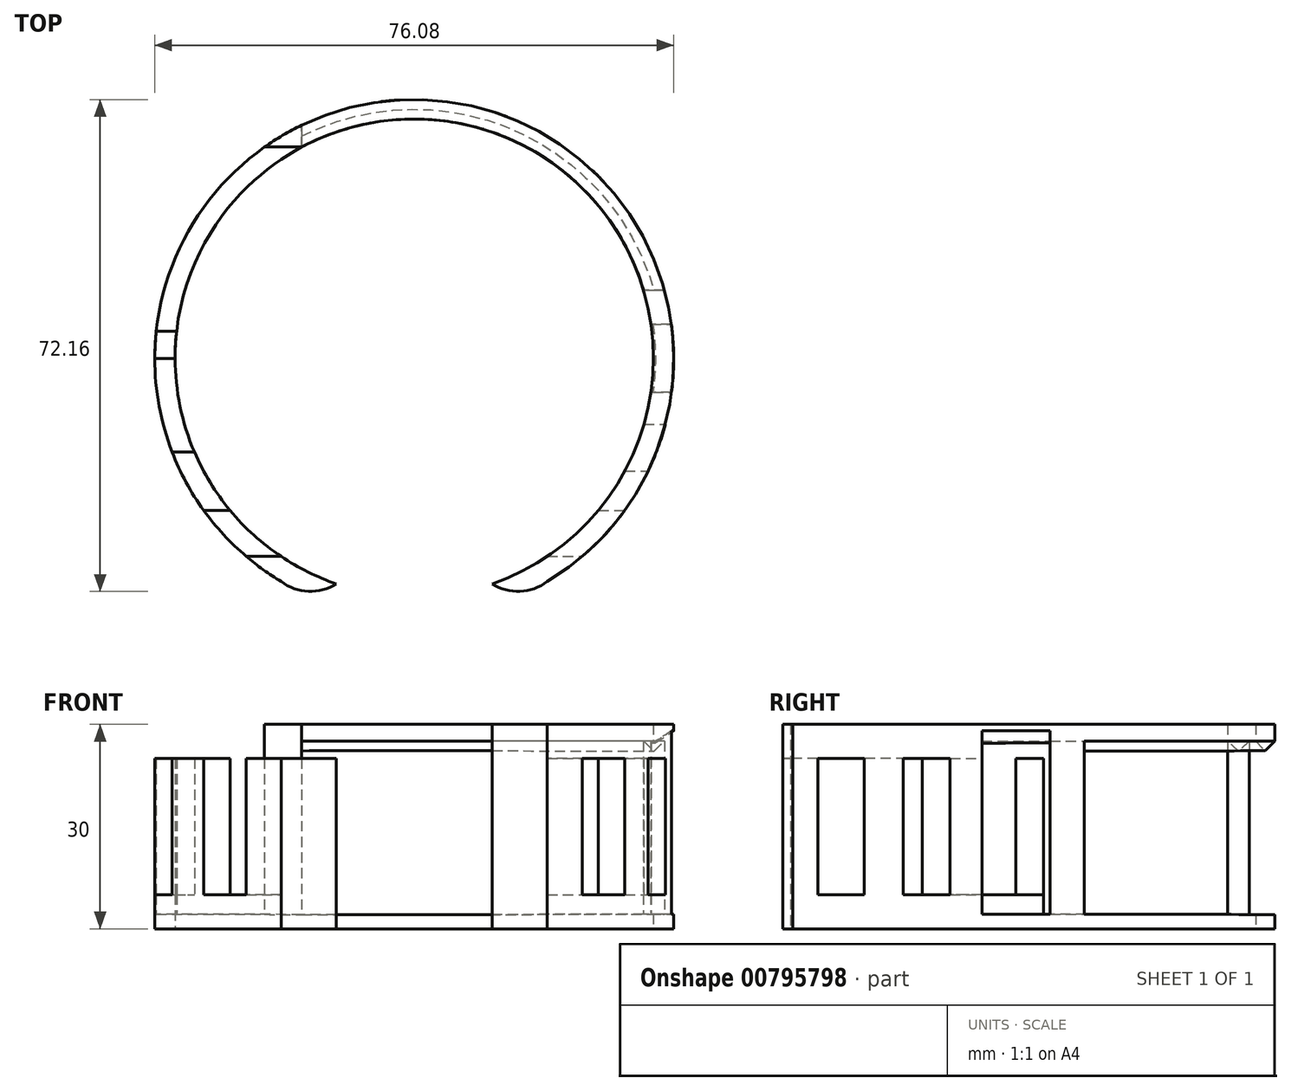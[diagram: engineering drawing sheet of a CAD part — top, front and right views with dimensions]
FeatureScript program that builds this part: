
annotation { "Feature Type Name" : "Feature", "Feature Type Description" : "" }
export const myFeature = defineFeature(function(context is Context, id is Id, definition is map)
    precondition{}
    {
        {
            var Q0;
            Q0=qCreatedBy(makeId("Top.planeOp"),FACE);
            var sketch = newSketch(context, id + "F0", { "sketchPlane" : qUnion([Q0])});
            skArc(sketch, "E0", {"start": v(11.43, -33.08) * mm, "mid": v(15.52, -34.19) * mm, "end": v(19.5, -32.73) * mm});
            skArc(sketch, "E1.MirrorCS", {"start": v(-11.43, -33.08) * mm, "mid": v(-15.52, -34.19) * mm, "end": v(-19.5, -32.73) * mm});
            skArc(sketch, "E2", {"start": v(11.43, -33.08) * mm, "mid": v(0, 35.12) * mm, "end": v(-11.43, -33.08) * mm});
            skArc(sketch, "E3", {"start": v(19.5, -32.73) * mm, "mid": v(0, 37.97) * mm, "end": v(-19.5, -32.73) * mm});
            skSolve(sketch);
        }
        {
            var Q0;
            Q0=makeQuery(id+"F0.imprint","IMPRINT",FACE,{"disambiguationData":[TD([[makeQuery(id+"F0.imprint","IMPRINT",EDGE,{"derivedFrom":sQuery(id+"F0.wireOp",EDGE,"E0")}),1.0]])]});
            extrude(context, id + "F1", {"entities" : qUnion([Q0]), "depth" : 5 * mm, "offsetDistance" : 25.4 * mm});
        }
        {
            var Q0;
            Q0=makeQuery(id+"F1.opExtrude","CAP_FACE",FACE,{"disambiguationData":[OSD([sQuery(id+"F0.wireOp",EDGE,"E0"),sQuery(id+"F0.wireOp",EDGE,"E1.MirrorCS"),sQuery(id+"F0.wireOp",EDGE,"E2"),sQuery(id+"F0.wireOp",EDGE,"E3")])],"isStart":false});
            var sketch = newSketch(context, id + "F2", { "sketchPlane" : qUnion([Q0])});
            skLineSegment(sketch, "E4", {"start": v(-38.04, 0) * mm, "end": v(-35.06, 0) * mm});
            skLineSegment(sketch, "E5", {"start": v(-37.82, 4) * mm, "end": v(-34.83, 4) * mm});
            skArc(sketch, "E6", {"start": v(-34.83, 4) * mm, "mid": v(-35.02, 2) * mm, "end": v(-35.06, 0) * mm});
            skArc(sketch, "E7", {"start": v(-37.82, 4) * mm, "mid": v(-37.97, 2) * mm, "end": v(-38.04, 0) * mm});
            skLineSegment(sketch, "E8", {"start": v(-21.95, 31) * mm, "end": v(-16.48, 31) * mm});
            skLineSegment(sketch, "E9", {"start": v(34.7, 5) * mm, "end": v(37.7, 5) * mm});
            skLineSegment(sketch, "E10", {"start": v(34.69, -5) * mm, "end": v(37.72, -5) * mm});
            skLineSegment(sketch, "E11", {"start": v(33.62, 10) * mm, "end": v(36.68, 10) * mm});
            skArc(sketch, "E12", {"start": v(37.7, 5) * mm, "mid": v(37.3, 7.52) * mm, "end": v(36.68, 10) * mm});
            skArc(sketch, "E13", {"start": v(34.7, 5) * mm, "mid": v(34.26, 7.52) * mm, "end": v(33.62, 10) * mm});
            skLineSegment(sketch, "E14", {"start": v(-16.48, 31) * mm, "end": v(-16.48, 34.21) * mm});
            skArc(sketch, "E15", {"start": v(-16.48, 34.21) * mm, "mid": v(-19.3, 32.77) * mm, "end": v(-21.95, 31) * mm});
            skLineSegment(sketch, "E16", {"start": v(33.68, -9.67) * mm, "end": v(36.8, -9.67) * mm});
            skArc(sketch, "E17", {"start": v(33.68, -9.67) * mm, "mid": v(34.3, -7.36) * mm, "end": v(34.69, -5) * mm});
            skArc(sketch, "E18", {"start": v(36.8, -9.67) * mm, "mid": v(37.38, -7.36) * mm, "end": v(37.72, -5) * mm});
            skLineSegment(sketch, "E19", {"start": v(-19.5, -29.07) * mm, "end": v(-24.61, -29.07) * mm});
            skLineSegment(sketch, "E20", {"start": v(19.5, -29.07) * mm, "end": v(24.61, -29.07) * mm});
            skLineSegment(sketch, "E21", {"start": v(-30.88, -22.29) * mm, "end": v(-27, -22.29) * mm});
            skLineSegment(sketch, "E22", {"start": v(27, -22.29) * mm, "end": v(30.88, -22.29) * mm});
            skLineSegment(sketch, "E23", {"start": v(-35.49, -13.77) * mm, "end": v(-32.21, -13.77) * mm});
            skLineSegment(sketch, "E24", {"start": v(30.88, -16.54) * mm, "end": v(34.29, -16.54) * mm});
            skSolve(sketch);
        }
        {
            var Q0;
            {var subQ0=sQuery(id+"F2.wireOp",EDGE,"E8");Q0=makeQuery(id+"F2.imprint","IMPRINT",FACE,{"disambiguationData":[TD([[makeQuery(id+"F2.imprint","IMPRINT",EDGE,{"derivedFrom":subQ0}),1.0]])]});}
            var Q1;
            Q1=makeQuery(id+"F2.imprint","IMPRINT",FACE,{"disambiguationData":[TD([[makeQuery(id+"F2.imprint","IMPRINT",EDGE,{"derivedFrom":sQuery(id+"F2.wireOp",EDGE,"E4")}),1.0]])]});
            var Q2;
            {var subQ0=sQuery(id+"F2.wireOp",EDGE,"E9");Q2=makeQuery(id+"F2.imprint","IMPRINT",FACE,{"disambiguationData":[TD([[makeQuery(id+"F2.imprint","IMPRINT",EDGE,{"derivedFrom":subQ0}),1.0]])]});}
            var Q3;
            {var subQ0=sQuery(id+"F2.wireOp",EDGE,"E10");Q3=makeQuery(id+"F2.imprint","IMPRINT",FACE,{"disambiguationData":[TD([[makeQuery(id+"F2.imprint","IMPRINT",EDGE,{"derivedFrom":subQ0}),-1.0]])]});}
            var Q4;
            {var subQ0=sQuery(id+"F2.wireOp",EDGE,"E19");Q4=makeQuery(id+"F2.imprint","IMPRINT",FACE,{"disambiguationData":[TD([[makeQuery(id+"F2.imprint","IMPRINT",EDGE,{"derivedFrom":subQ0}),1.0]])]});}
            var Q5;
            {var subQ0=sQuery(id+"F2.wireOp",EDGE,"E20");Q5=makeQuery(id+"F2.imprint","IMPRINT",FACE,{"disambiguationData":[TD([[makeQuery(id+"F2.imprint","IMPRINT",EDGE,{"derivedFrom":subQ0}),-1.0]])]});}
            var Q6;
            {var subQ0=sQuery(id+"F2.wireOp",EDGE,"E22");Q6=makeQuery(id+"F2.imprint","IMPRINT",FACE,{"disambiguationData":[TD([[makeQuery(id+"F2.imprint","IMPRINT",EDGE,{"derivedFrom":subQ0}),1.0]])]});}
            var Q7;
            {var subQ0=sQuery(id+"F2.wireOp",EDGE,"E21");Q7=makeQuery(id+"F2.imprint","IMPRINT",FACE,{"disambiguationData":[TD([[makeQuery(id+"F2.imprint","IMPRINT",EDGE,{"derivedFrom":subQ0}),1.0]])]});}
            extrude(context, id + "F3", {"entities" : qUnion([Q0, Q1, Q2, Q3, Q4, Q5, Q6, Q7]), "operationType" : NewBodyOperationType.ADD, "depth" : 20 * mm, "offsetDistance" : 25.4 * mm});
        }
        {
            var Q0;
            Q0=makeQuery(id+"F3.opExtrude","CAP_FACE",FACE,{"disambiguationData":[OSD([sQuery(id+"F0.wireOp",EDGE,"E2"),sQuery(id+"F0.wireOp",EDGE,"E3"),sQuery(id+"F2.wireOp",EDGE,"E8"),sQuery(id+"F2.wireOp",EDGE,"E11")])],"isStart":false});
            var sketch = newSketch(context, id + "F4", { "sketchPlane" : qUnion([Q0])});
            skArc(sketch, "E25", {"start": v(11.43, -33.08) * mm, "mid": v(15.52, -34.19) * mm, "end": v(19.5, -32.73) * mm});
            skArc(sketch, "E26.MirrorCS", {"start": v(-11.43, -33.08) * mm, "mid": v(-15.52, -34.19) * mm, "end": v(-19.5, -32.73) * mm});
            skArc(sketch, "E27", {"start": v(11.43, -33.08) * mm, "mid": v(0, 35.12) * mm, "end": v(-11.43, -33.08) * mm});
            skArc(sketch, "E28", {"start": v(19.5, -32.73) * mm, "mid": v(0, 37.97) * mm, "end": v(-19.5, -32.73) * mm});
            skSolve(sketch);
        }
        {
            var Q0;
            {var subQ0=sQuery(id+"F4.wireOp",EDGE,"E25");Q0=makeQuery(id+"F4.imprint","IMPRINT",FACE,{"disambiguationData":[TD([[makeQuery(id+"F4.imprint","IMPRINT",EDGE,{"derivedFrom":subQ0}),1.0]])]});}
            var Q1;
            {var subQ1=makeQuery(id+"F3.opExtrude","CAP_EDGE",EDGE,{"disambiguationData":[OSD([sQuery(id+"F2.wireOp",EDGE,"E8")])],"isStart":false});Q1=makeQuery(id+"F4.imprint","IMPRINT",FACE,{"disambiguationData":[TD([[makeQuery(id+"F4.imprint","IMPRINT",EDGE,{"derivedFrom":subQ1}),1.0]])]});}
            var Q2;
            {var subQ0=sQuery(id+"F4.wireOp",EDGE,"E26.MirrorCS");Q2=makeQuery(id+"F4.imprint","IMPRINT",FACE,{"disambiguationData":[TD([[makeQuery(id+"F4.imprint","IMPRINT",EDGE,{"derivedFrom":subQ0}),-1.0]])]});}
            extrude(context, id + "F5", {"entities" : qUnion([Q0, Q1, Q2]), "operationType" : NewBodyOperationType.ADD, "depth" : 5 * mm, "offsetDistance" : 25.4 * mm});
        }
        {
            var Q0;
            {var subQ0=sQuery(id+"F2.wireOp",EDGE,"E8");var subQ1=sQuery(id+"F4.wireOp",EDGE,"E28");var subQ2=makeQuery(id+"F4.imprint","INTERSECT",VERTEX,{"derivedFrom":[makeQuery(id+"F3.opExtrude","CAP_EDGE",EDGE,{"disambiguationData":[OSD([subQ0])],"isStart":false}),subQ1]});var subQ3=sQuery(id+"F4.wireOp",EDGE,"E26.MirrorCS");var subQ4=makeQuery(id+"F4.imprint","IMPRINT",EDGE,{"disambiguationData":[TD([[subQ2,-1.0]])],"derivedFrom":subQ1});var subQ5=sQuery(id+"F0.wireOp",EDGE,"E3");var subQ7=sQuery(id+"F2.wireOp",EDGE,"E15");var subQ8=makeQuery(id+"F1.opExtrude","CAP_EDGE",EDGE,{"disambiguationData":[OSD([subQ5])],"isStart":false});var subQ9=sQuery(id+"F2.wireOp",EDGE,"E12");var subQ10=sQuery(id+"F2.wireOp",EDGE,"E18");Q0=makeQuery(id+"F5.boolean.opBoolean","SPLIT",EDGE,{"disambiguationData":[TD([makeQuery(id+"F1.opExtrude","SWEPT_FACE",FACE,{"disambiguationData":[OSD([subQ5])]}),makeQuery(id+"F3.opExtrude","SWEPT_FACE",FACE,{"disambiguationData":[OSD([sQuery(id+"F2.wireOp",EDGE,"E5")])]}),makeQuery(id+"F3.opExtrude","SWEPT_FACE",FACE,{"disambiguationData":[OSD([sQuery(id+"F2.wireOp",EDGE,"E7")])]}),makeQuery(id+"F3.opExtrude","SWEPT_FACE",FACE,{"disambiguationData":[OSD([subQ0])]}),makeQuery(id+"F3.opExtrude","SWEPT_FACE",FACE,{"disambiguationData":[OSD([subQ5]),TDD([makeQuery(id+"F2.imprint","IMPRINT",EDGE,{"disambiguationData":[TD([[makeQuery(id+"F2.imprint","INTERSECT",VERTEX,{"derivedFrom":[subQ8,subQ0,subQ7]}),1.0]])],"derivedFrom":subQ8})])]}),makeQuery(id+"F3.opExtrude","SWEPT_FACE",FACE,{"disambiguationData":[OSD([subQ5]),TDD([makeQuery(id+"F2.imprint","IMPRINT",EDGE,{"disambiguationData":[TD([[makeQuery(id+"F2.imprint","INTERSECT",VERTEX,{"derivedFrom":[subQ8,sQuery(id+"F2.wireOp",EDGE,"E9"),subQ9]}),-1.0]])],"derivedFrom":subQ8})])]}),makeQuery(id+"F3.opExtrude","SWEPT_FACE",FACE,{"disambiguationData":[OSD([subQ5]),TDD([makeQuery(id+"F2.imprint","IMPRINT",EDGE,{"disambiguationData":[TD([[makeQuery(id+"F2.imprint","INTERSECT",VERTEX,{"derivedFrom":[subQ8,sQuery(id+"F2.wireOp",EDGE,"E10"),subQ10]}),1.0]])],"derivedFrom":subQ8})])]}),makeQuery(id+"F5.opExtrude","CAP_FACE",FACE,{"disambiguationData":[OSD([sQuery(id+"F4.wireOp",EDGE,"E25"),subQ3,sQuery(id+"F4.wireOp",EDGE,"E27"),subQ1])],"isStart":true}),makeQuery(id+"F5.opExtrude","SWEPT_FACE",FACE,{"disambiguationData":[OSD([subQ1]),TDD([makeQuery(id+"F4.imprint","IMPRINT",EDGE,{"disambiguationData":[TD([[subQ2,1.0]])],"derivedFrom":subQ1})])]}),makeQuery(id+"F5.opExtrude","SWEPT_FACE",FACE,{"disambiguationData":[OSD([subQ1]),TDD([subQ4])]})])],"derivedFrom":makeQuery(id+"F5.opExtrude","CAP_EDGE",EDGE,{"disambiguationData":[OSD([subQ1]),TDD([subQ4])],"isStart":true})});}
            var Q1;
            {var subQ0=sQuery(id+"F0.wireOp",EDGE,"E3");var subQ1=sQuery(id+"F2.wireOp",EDGE,"E8");var subQ2=sQuery(id+"F2.wireOp",EDGE,"E15");var subQ3=makeQuery(id+"F1.opExtrude","CAP_EDGE",EDGE,{"disambiguationData":[OSD([subQ0])],"isStart":false});var subQ4=sQuery(id+"F2.wireOp",EDGE,"E12");var subQ5=sQuery(id+"F2.wireOp",EDGE,"E18");Q1=makeQuery(id+"F3.boolean.opBoolean","SPLIT",EDGE,{"disambiguationData":[TD([makeQuery(id+"F1.opExtrude","CAP_FACE",FACE,{"disambiguationData":[OSD([sQuery(id+"F0.wireOp",EDGE,"E0"),sQuery(id+"F0.wireOp",EDGE,"E1.MirrorCS"),sQuery(id+"F0.wireOp",EDGE,"E2"),subQ0])],"isStart":false}),makeQuery(id+"F1.opExtrude","SWEPT_FACE",FACE,{"disambiguationData":[OSD([subQ0])]}),makeQuery(id+"F3.opExtrude","SWEPT_FACE",FACE,{"disambiguationData":[OSD([sQuery(id+"F2.wireOp",EDGE,"E5")])]}),makeQuery(id+"F3.opExtrude","SWEPT_FACE",FACE,{"disambiguationData":[OSD([sQuery(id+"F2.wireOp",EDGE,"E7")])]}),makeQuery(id+"F3.opExtrude","SWEPT_FACE",FACE,{"disambiguationData":[OSD([subQ1])]}),makeQuery(id+"F3.opExtrude","SWEPT_FACE",FACE,{"disambiguationData":[OSD([subQ0]),TDD([makeQuery(id+"F2.imprint","IMPRINT",EDGE,{"disambiguationData":[TD([[makeQuery(id+"F2.imprint","INTERSECT",VERTEX,{"derivedFrom":[subQ3,subQ1,subQ2]}),1.0]])],"derivedFrom":subQ3})])]}),makeQuery(id+"F3.opExtrude","SWEPT_FACE",FACE,{"disambiguationData":[OSD([subQ0]),TDD([makeQuery(id+"F2.imprint","IMPRINT",EDGE,{"disambiguationData":[TD([[makeQuery(id+"F2.imprint","INTERSECT",VERTEX,{"derivedFrom":[subQ3,sQuery(id+"F2.wireOp",EDGE,"E9"),subQ4]}),-1.0]])],"derivedFrom":subQ3})])]}),makeQuery(id+"F3.opExtrude","SWEPT_FACE",FACE,{"disambiguationData":[OSD([subQ0]),TDD([makeQuery(id+"F2.imprint","IMPRINT",EDGE,{"disambiguationData":[TD([[makeQuery(id+"F2.imprint","INTERSECT",VERTEX,{"derivedFrom":[subQ3,sQuery(id+"F2.wireOp",EDGE,"E10"),subQ5]}),1.0]])],"derivedFrom":subQ3})])]})])],"derivedFrom":subQ3});}
            var Q2;
            {var subQ0=sQuery(id+"F4.wireOp",EDGE,"E27");Q2=makeQuery(id+"F5.boolean.opBoolean","SPLIT",EDGE,{"disambiguationData":[TD([makeQuery(id+"F3.opExtrude","SWEPT_FACE",FACE,{"disambiguationData":[OSD([sQuery(id+"F2.wireOp",EDGE,"E5")])]}),makeQuery(id+"F3.opExtrude","SWEPT_FACE",FACE,{"disambiguationData":[OSD([sQuery(id+"F2.wireOp",EDGE,"E6")])]}),makeQuery(id+"F3.opExtrude","SWEPT_FACE",FACE,{"disambiguationData":[OSD([sQuery(id+"F2.wireOp",EDGE,"E8")])]}),makeQuery(id+"F3.opExtrude","SWEPT_FACE",FACE,{"disambiguationData":[OSD([sQuery(id+"F2.wireOp",EDGE,"E14")])]}),makeQuery(id+"F5.opExtrude","CAP_FACE",FACE,{"disambiguationData":[OSD([sQuery(id+"F4.wireOp",EDGE,"E25"),sQuery(id+"F4.wireOp",EDGE,"E26.MirrorCS"),subQ0,sQuery(id+"F4.wireOp",EDGE,"E28")])],"isStart":true}),makeQuery(id+"F5.opExtrude","SWEPT_FACE",FACE,{"disambiguationData":[OSD([subQ0])]})])],"derivedFrom":makeQuery(id+"F5.opExtrude","CAP_EDGE",EDGE,{"disambiguationData":[OSD([subQ0])],"isStart":true})});}
            var Q3;
            {var subQ0=sQuery(id+"F0.wireOp",EDGE,"E2");Q3=makeQuery(id+"F3.boolean.opBoolean","SPLIT",EDGE,{"disambiguationData":[TD([makeQuery(id+"F1.opExtrude","CAP_FACE",FACE,{"disambiguationData":[OSD([sQuery(id+"F0.wireOp",EDGE,"E0"),sQuery(id+"F0.wireOp",EDGE,"E1.MirrorCS"),subQ0,sQuery(id+"F0.wireOp",EDGE,"E3")])],"isStart":false}),makeQuery(id+"F1.opExtrude","SWEPT_FACE",FACE,{"disambiguationData":[OSD([subQ0])]}),makeQuery(id+"F3.opExtrude","SWEPT_FACE",FACE,{"disambiguationData":[OSD([sQuery(id+"F2.wireOp",EDGE,"E5")])]}),makeQuery(id+"F3.opExtrude","SWEPT_FACE",FACE,{"disambiguationData":[OSD([sQuery(id+"F2.wireOp",EDGE,"E6")])]}),makeQuery(id+"F3.opExtrude","SWEPT_FACE",FACE,{"disambiguationData":[OSD([sQuery(id+"F2.wireOp",EDGE,"E8")])]}),makeQuery(id+"F3.opExtrude","SWEPT_FACE",FACE,{"disambiguationData":[OSD([sQuery(id+"F2.wireOp",EDGE,"E14")])]})])],"derivedFrom":makeQuery(id+"F1.opExtrude","CAP_EDGE",EDGE,{"disambiguationData":[OSD([subQ0])],"isStart":false})});}
            chamfer(context, id + "F6", {"entities" : qUnion([Q0, Q1, Q2, Q3]), "width" : 2.54 * mm, "tangentPropagation" : true});
        }
        {
            var Q0;
            {var subQ0=sQuery(id+"F2.wireOp",EDGE,"E8");var subQ1=makeQuery(id+"F3.opExtrude","SWEPT_FACE",FACE,{"disambiguationData":[OSD([subQ0])]});var subQ2=sQuery(id+"F4.wireOp",EDGE,"E28");var subQ3=makeQuery(id+"F4.imprint","INTERSECT",VERTEX,{"derivedFrom":[makeQuery(id+"F3.opExtrude","CAP_EDGE",EDGE,{"disambiguationData":[OSD([subQ0])],"isStart":false}),subQ2]});var subQ4=sQuery(id+"F4.wireOp",EDGE,"E26.MirrorCS");var subQ5=makeQuery(id+"F4.imprint","IMPRINT",EDGE,{"disambiguationData":[TD([[subQ3,-1.0]])],"derivedFrom":subQ2});var subQ6=makeQuery(id+"F3.opExtrude","SWEPT_FACE",FACE,{"disambiguationData":[OSD([sQuery(id+"F2.wireOp",EDGE,"E5")])]});var subQ7=sQuery(id+"F0.wireOp",EDGE,"E3");var subQ8=sQuery(id+"F2.wireOp",EDGE,"E14");var subQ9=sQuery(id+"F2.wireOp",EDGE,"E15");var subQ10=makeQuery(id+"F1.opExtrude","CAP_EDGE",EDGE,{"disambiguationData":[OSD([subQ7])],"isStart":false});var subQ11=sQuery(id+"F2.wireOp",EDGE,"E12");var subQ12=sQuery(id+"F4.wireOp",EDGE,"E27");var subQ13=makeQuery(id+"F5.opExtrude","CAP_FACE",FACE,{"disambiguationData":[OSD([sQuery(id+"F4.wireOp",EDGE,"E25"),subQ4,subQ12,subQ2])],"isStart":true});var subQ14=sQuery(id+"F2.wireOp",EDGE,"E18");Q0=makeQuery(id+"F6.opChamfer","BLEND_EDGE",EDGE,{"blendedFrom":[makeQuery(id+"F5.boolean.opBoolean","SPLIT",EDGE,{"disambiguationData":[TD([subQ6,makeQuery(id+"F3.opExtrude","SWEPT_FACE",FACE,{"disambiguationData":[OSD([sQuery(id+"F2.wireOp",EDGE,"E6")])]}),subQ1,makeQuery(id+"F3.opExtrude","SWEPT_FACE",FACE,{"disambiguationData":[OSD([subQ8])]}),subQ13,makeQuery(id+"F5.opExtrude","SWEPT_FACE",FACE,{"disambiguationData":[OSD([subQ12])]})])],"derivedFrom":makeQuery(id+"F5.opExtrude","CAP_EDGE",EDGE,{"disambiguationData":[OSD([subQ12])],"isStart":true})}),makeQuery(id+"F5.boolean.opBoolean","SPLIT",EDGE,{"disambiguationData":[TD([makeQuery(id+"F1.opExtrude","SWEPT_FACE",FACE,{"disambiguationData":[OSD([subQ7])]}),subQ6,makeQuery(id+"F3.opExtrude","SWEPT_FACE",FACE,{"disambiguationData":[OSD([sQuery(id+"F2.wireOp",EDGE,"E7")])]}),subQ1,makeQuery(id+"F3.opExtrude","SWEPT_FACE",FACE,{"disambiguationData":[OSD([subQ7]),TDD([makeQuery(id+"F2.imprint","IMPRINT",EDGE,{"disambiguationData":[TD([[makeQuery(id+"F2.imprint","INTERSECT",VERTEX,{"derivedFrom":[subQ10,subQ0,subQ9]}),1.0]])],"derivedFrom":subQ10})])]}),makeQuery(id+"F3.opExtrude","SWEPT_FACE",FACE,{"disambiguationData":[OSD([subQ7]),TDD([makeQuery(id+"F2.imprint","IMPRINT",EDGE,{"disambiguationData":[TD([[makeQuery(id+"F2.imprint","INTERSECT",VERTEX,{"derivedFrom":[subQ10,sQuery(id+"F2.wireOp",EDGE,"E9"),subQ11]}),-1.0]])],"derivedFrom":subQ10})])]}),makeQuery(id+"F3.opExtrude","SWEPT_FACE",FACE,{"disambiguationData":[OSD([subQ7]),TDD([makeQuery(id+"F2.imprint","IMPRINT",EDGE,{"disambiguationData":[TD([[makeQuery(id+"F2.imprint","INTERSECT",VERTEX,{"derivedFrom":[subQ10,sQuery(id+"F2.wireOp",EDGE,"E10"),subQ14]}),1.0]])],"derivedFrom":subQ10})])]}),subQ13,makeQuery(id+"F5.opExtrude","SWEPT_FACE",FACE,{"disambiguationData":[OSD([subQ2]),TDD([makeQuery(id+"F4.imprint","IMPRINT",EDGE,{"disambiguationData":[TD([[subQ3,1.0]])],"derivedFrom":subQ2})])]}),makeQuery(id+"F5.opExtrude","SWEPT_FACE",FACE,{"disambiguationData":[OSD([subQ2]),TDD([subQ5])]})])],"derivedFrom":makeQuery(id+"F5.opExtrude","CAP_EDGE",EDGE,{"disambiguationData":[OSD([subQ2]),TDD([subQ5])],"isStart":true})})],"blendedInto":[]});}
            var Q1;
            {var subQ0=makeQuery(id+"F3.opExtrude","SWEPT_FACE",FACE,{"disambiguationData":[OSD([sQuery(id+"F2.wireOp",EDGE,"E5")])]});var subQ1=sQuery(id+"F0.wireOp",EDGE,"E3");var subQ2=sQuery(id+"F0.wireOp",EDGE,"E2");var subQ3=makeQuery(id+"F1.opExtrude","CAP_FACE",FACE,{"disambiguationData":[OSD([sQuery(id+"F0.wireOp",EDGE,"E0"),sQuery(id+"F0.wireOp",EDGE,"E1.MirrorCS"),subQ2,subQ1])],"isStart":false});var subQ4=sQuery(id+"F2.wireOp",EDGE,"E8");var subQ5=makeQuery(id+"F3.opExtrude","SWEPT_FACE",FACE,{"disambiguationData":[OSD([subQ4])]});var subQ6=sQuery(id+"F2.wireOp",EDGE,"E15");var subQ7=makeQuery(id+"F1.opExtrude","CAP_EDGE",EDGE,{"disambiguationData":[OSD([subQ1])],"isStart":false});var subQ8=sQuery(id+"F2.wireOp",EDGE,"E14");var subQ9=sQuery(id+"F2.wireOp",EDGE,"E12");var subQ10=sQuery(id+"F2.wireOp",EDGE,"E18");Q1=makeQuery(id+"F6.opChamfer","BLEND_EDGE",EDGE,{"blendedFrom":[makeQuery(id+"F3.boolean.opBoolean","SPLIT",EDGE,{"disambiguationData":[TD([subQ3,makeQuery(id+"F1.opExtrude","SWEPT_FACE",FACE,{"disambiguationData":[OSD([subQ2])]}),subQ0,makeQuery(id+"F3.opExtrude","SWEPT_FACE",FACE,{"disambiguationData":[OSD([sQuery(id+"F2.wireOp",EDGE,"E6")])]}),subQ5,makeQuery(id+"F3.opExtrude","SWEPT_FACE",FACE,{"disambiguationData":[OSD([subQ8])]})])],"derivedFrom":makeQuery(id+"F1.opExtrude","CAP_EDGE",EDGE,{"disambiguationData":[OSD([subQ2])],"isStart":false})}),makeQuery(id+"F3.boolean.opBoolean","SPLIT",EDGE,{"disambiguationData":[TD([subQ3,makeQuery(id+"F1.opExtrude","SWEPT_FACE",FACE,{"disambiguationData":[OSD([subQ1])]}),subQ0,makeQuery(id+"F3.opExtrude","SWEPT_FACE",FACE,{"disambiguationData":[OSD([sQuery(id+"F2.wireOp",EDGE,"E7")])]}),subQ5,makeQuery(id+"F3.opExtrude","SWEPT_FACE",FACE,{"disambiguationData":[OSD([subQ1]),TDD([makeQuery(id+"F2.imprint","IMPRINT",EDGE,{"disambiguationData":[TD([[makeQuery(id+"F2.imprint","INTERSECT",VERTEX,{"derivedFrom":[subQ7,subQ4,subQ6]}),1.0]])],"derivedFrom":subQ7})])]}),makeQuery(id+"F3.opExtrude","SWEPT_FACE",FACE,{"disambiguationData":[OSD([subQ1]),TDD([makeQuery(id+"F2.imprint","IMPRINT",EDGE,{"disambiguationData":[TD([[makeQuery(id+"F2.imprint","INTERSECT",VERTEX,{"derivedFrom":[subQ7,sQuery(id+"F2.wireOp",EDGE,"E9"),subQ9]}),-1.0]])],"derivedFrom":subQ7})])]}),makeQuery(id+"F3.opExtrude","SWEPT_FACE",FACE,{"disambiguationData":[OSD([subQ1]),TDD([makeQuery(id+"F2.imprint","IMPRINT",EDGE,{"disambiguationData":[TD([[makeQuery(id+"F2.imprint","INTERSECT",VERTEX,{"derivedFrom":[subQ7,sQuery(id+"F2.wireOp",EDGE,"E10"),subQ10]}),1.0]])],"derivedFrom":subQ7})])]})])],"derivedFrom":subQ7})],"blendedInto":[]});}
            chamfer(context, id + "F7", {"entities" : qUnion([Q0, Q1]), "width" : 2.54 * mm, "tangentPropagation" : true});
        }
        {
            var Q0;
            {var subQ0=sQuery(id+"F0.wireOp",EDGE,"E2");var subQ1=makeQuery(id+"F1.opExtrude","CAP_EDGE",EDGE,{"disambiguationData":[OSD([subQ0])],"isStart":false});var subQ2=sQuery(id+"F0.wireOp",EDGE,"E1.MirrorCS");var subQ3=sQuery(id+"F0.wireOp",EDGE,"E0");Q0=makeQuery(id+"F3.boolean.opBoolean","SPLIT",EDGE,{"disambiguationData":[TD([makeQuery(id+"F1.opExtrude","CAP_FACE",FACE,{"disambiguationData":[OSD([subQ3,subQ2,subQ0,sQuery(id+"F0.wireOp",EDGE,"E3")])],"isStart":false}),makeQuery(id+"F1.opExtrude","SWEPT_FACE",FACE,{"disambiguationData":[OSD([subQ0])]}),makeQuery(id+"F3.opExtrude","SWEPT_FACE",FACE,{"disambiguationData":[OSD([sQuery(id+"F2.wireOp",EDGE,"E8")])]}),makeQuery(id+"F3.opExtrude","SWEPT_FACE",FACE,{"disambiguationData":[OSD([sQuery(id+"F2.wireOp",EDGE,"E11")])]}),makeQuery(id+"F3.opExtrude","SWEPT_FACE",FACE,{"disambiguationData":[OSD([sQuery(id+"F2.wireOp",EDGE,"E13")])]}),makeQuery(id+"F3.opExtrude","SWEPT_FACE",FACE,{"disambiguationData":[OSD([sQuery(id+"F2.wireOp",EDGE,"E14")])]}),makeQuery(id+"F3.opExtrude","SWEPT_FACE",FACE,{"disambiguationData":[OSD([subQ0]),TDD([makeQuery(id+"F2.imprint","IMPRINT",EDGE,{"disambiguationData":[TD([[makeQuery(id+"F2.imprint","INTERSECT",VERTEX,{"derivedFrom":[makeQuery(id+"F1.opExtrude","CAP_EDGE",EDGE,{"disambiguationData":[OSD([subQ3])],"isStart":false}),subQ1]}),-1.0]])],"derivedFrom":subQ1})])]}),makeQuery(id+"F3.opExtrude","SWEPT_FACE",FACE,{"disambiguationData":[OSD([subQ0]),TDD([makeQuery(id+"F2.imprint","IMPRINT",EDGE,{"disambiguationData":[TD([[makeQuery(id+"F2.imprint","INTERSECT",VERTEX,{"derivedFrom":[makeQuery(id+"F1.opExtrude","CAP_EDGE",EDGE,{"disambiguationData":[OSD([subQ2])],"isStart":false}),subQ1]}),1.0]])],"derivedFrom":subQ1})])]}),makeQuery(id+"F3.opExtrude","SWEPT_FACE",FACE,{"disambiguationData":[OSD([subQ0]),TDD([makeQuery(id+"F2.imprint","IMPRINT",EDGE,{"disambiguationData":[TD([[makeQuery(id+"F2.imprint","INTERSECT",VERTEX,{"derivedFrom":[subQ1,sQuery(id+"F2.wireOp",EDGE,"E21")]}),1.0]])],"derivedFrom":subQ1})])]}),makeQuery(id+"F3.opExtrude","SWEPT_FACE",FACE,{"disambiguationData":[OSD([subQ0]),TDD([makeQuery(id+"F2.imprint","IMPRINT",EDGE,{"disambiguationData":[TD([[makeQuery(id+"F2.imprint","INTERSECT",VERTEX,{"derivedFrom":[subQ1,sQuery(id+"F2.wireOp",EDGE,"E22")]}),-1.0]])],"derivedFrom":subQ1})])]})])],"derivedFrom":subQ1});}
            var Q1;
            {var subQ0=sQuery(id+"F0.wireOp",EDGE,"E2");var subQ1=sQuery(id+"F0.wireOp",EDGE,"E1.MirrorCS");var subQ2=sQuery(id+"F0.wireOp",EDGE,"E0");var subQ3=makeQuery(id+"F1.opExtrude","CAP_EDGE",EDGE,{"disambiguationData":[OSD([subQ0])],"isStart":false});Q1=makeQuery(id+"F3.boolean.opBoolean","SPLIT",EDGE,{"disambiguationData":[TD([makeQuery(id+"F1.opExtrude","CAP_FACE",FACE,{"disambiguationData":[OSD([subQ2,subQ1,subQ0,sQuery(id+"F0.wireOp",EDGE,"E3")])],"isStart":false}),makeQuery(id+"F1.opExtrude","SWEPT_FACE",FACE,{"disambiguationData":[OSD([subQ0])]}),makeQuery(id+"F3.opExtrude","SWEPT_FACE",FACE,{"disambiguationData":[OSD([sQuery(id+"F2.wireOp",EDGE,"E9")])]}),makeQuery(id+"F3.opExtrude","SWEPT_FACE",FACE,{"disambiguationData":[OSD([sQuery(id+"F2.wireOp",EDGE,"E10")])]}),makeQuery(id+"F3.opExtrude","SWEPT_FACE",FACE,{"disambiguationData":[OSD([sQuery(id+"F2.wireOp",EDGE,"E13")])]}),makeQuery(id+"F3.opExtrude","SWEPT_FACE",FACE,{"disambiguationData":[OSD([sQuery(id+"F2.wireOp",EDGE,"E17")])]}),makeQuery(id+"F3.opExtrude","SWEPT_FACE",FACE,{"disambiguationData":[OSD([subQ0]),TDD([makeQuery(id+"F2.imprint","IMPRINT",EDGE,{"disambiguationData":[TD([[makeQuery(id+"F2.imprint","INTERSECT",VERTEX,{"derivedFrom":[makeQuery(id+"F1.opExtrude","CAP_EDGE",EDGE,{"disambiguationData":[OSD([subQ2])],"isStart":false}),subQ3]}),-1.0]])],"derivedFrom":subQ3})])]}),makeQuery(id+"F3.opExtrude","SWEPT_FACE",FACE,{"disambiguationData":[OSD([subQ0]),TDD([makeQuery(id+"F2.imprint","IMPRINT",EDGE,{"disambiguationData":[TD([[makeQuery(id+"F2.imprint","INTERSECT",VERTEX,{"derivedFrom":[makeQuery(id+"F1.opExtrude","CAP_EDGE",EDGE,{"disambiguationData":[OSD([subQ1])],"isStart":false}),subQ3]}),1.0]])],"derivedFrom":subQ3})])]}),makeQuery(id+"F3.opExtrude","SWEPT_FACE",FACE,{"disambiguationData":[OSD([subQ0]),TDD([makeQuery(id+"F2.imprint","IMPRINT",EDGE,{"disambiguationData":[TD([[makeQuery(id+"F2.imprint","INTERSECT",VERTEX,{"derivedFrom":[subQ3,sQuery(id+"F2.wireOp",EDGE,"E21")]}),1.0]])],"derivedFrom":subQ3})])]}),makeQuery(id+"F3.opExtrude","SWEPT_FACE",FACE,{"disambiguationData":[OSD([subQ0]),TDD([makeQuery(id+"F2.imprint","IMPRINT",EDGE,{"disambiguationData":[TD([[makeQuery(id+"F2.imprint","INTERSECT",VERTEX,{"derivedFrom":[subQ3,sQuery(id+"F2.wireOp",EDGE,"E22")]}),-1.0]])],"derivedFrom":subQ3})])]})])],"derivedFrom":subQ3});}
            chamfer(context, id + "F8", {"entities" : qUnion([Q0, Q1]), "width" : 2.54 * mm, "tangentPropagation" : true});
        }
        {
            var Q0;
            {var subQ4=sQuery(id+"F2.wireOp",EDGE,"E11");var subQ7=sQuery(id+"F2.wireOp",EDGE,"E14");var subQ8=sQuery(id+"F4.wireOp",EDGE,"E28");var subQ9=makeQuery(id+"F4.imprint","INTERSECT",VERTEX,{"derivedFrom":[makeQuery(id+"F3.opExtrude","CAP_EDGE",EDGE,{"disambiguationData":[OSD([subQ7])],"isStart":false}),subQ8]});var subQ11=makeQuery(id+"F4.imprint","IMPRINT",EDGE,{"disambiguationData":[TD([[subQ9,1.0]])],"derivedFrom":subQ8});Q0=makeQuery(id+"F5.boolean.opBoolean","SPLIT",EDGE,{"disambiguationData":[TD([makeQuery(id+"F3.opExtrude","SWEPT_FACE",FACE,{"disambiguationData":[OSD([subQ4])]})])],"derivedFrom":makeQuery(id+"F5.opExtrude","CAP_EDGE",EDGE,{"disambiguationData":[OSD([subQ8]),TDD([subQ11])],"isStart":true})});}
            var Q1;
            {var subQ0=sQuery(id+"F2.wireOp",EDGE,"E15");var subQ1=sQuery(id+"F0.wireOp",EDGE,"E3");var subQ2=makeQuery(id+"F1.opExtrude","CAP_EDGE",EDGE,{"disambiguationData":[OSD([subQ1])],"isStart":false});var subQ3=sQuery(id+"F2.wireOp",EDGE,"E14");var subQ4=sQuery(id+"F0.wireOp",EDGE,"E1.MirrorCS");var subQ5=sQuery(id+"F0.wireOp",EDGE,"E0");var subQ6=sQuery(id+"F2.wireOp",EDGE,"E12");var subQ7=sQuery(id+"F2.wireOp",EDGE,"E11");var subQ8=sQuery(id+"F2.wireOp",EDGE,"E18");Q1=makeQuery(id+"F3.boolean.opBoolean","SPLIT",EDGE,{"disambiguationData":[TD([makeQuery(id+"F1.opExtrude","CAP_FACE",FACE,{"disambiguationData":[OSD([subQ5,subQ4,sQuery(id+"F0.wireOp",EDGE,"E2"),subQ1])],"isStart":false}),makeQuery(id+"F1.opExtrude","SWEPT_FACE",FACE,{"disambiguationData":[OSD([subQ1])]}),makeQuery(id+"F3.opExtrude","SWEPT_FACE",FACE,{"disambiguationData":[OSD([subQ7])]}),makeQuery(id+"F3.opExtrude","SWEPT_FACE",FACE,{"disambiguationData":[OSD([subQ3])]}),makeQuery(id+"F3.opExtrude","SWEPT_FACE",FACE,{"disambiguationData":[OSD([subQ1]),TDD([makeQuery(id+"F2.imprint","IMPRINT",EDGE,{"disambiguationData":[TD([[makeQuery(id+"F2.imprint","INTERSECT",VERTEX,{"derivedFrom":[makeQuery(id+"F1.opExtrude","CAP_EDGE",EDGE,{"disambiguationData":[OSD([subQ5])],"isStart":false}),subQ2]}),-1.0]])],"derivedFrom":subQ2})])]}),makeQuery(id+"F3.opExtrude","SWEPT_FACE",FACE,{"disambiguationData":[OSD([subQ1]),TDD([makeQuery(id+"F2.imprint","IMPRINT",EDGE,{"disambiguationData":[TD([[makeQuery(id+"F2.imprint","INTERSECT",VERTEX,{"derivedFrom":[makeQuery(id+"F1.opExtrude","CAP_EDGE",EDGE,{"disambiguationData":[OSD([subQ4])],"isStart":false}),subQ2]}),1.0]])],"derivedFrom":subQ2})])]}),makeQuery(id+"F3.opExtrude","SWEPT_FACE",FACE,{"disambiguationData":[OSD([subQ1]),TDD([makeQuery(id+"F2.imprint","IMPRINT",EDGE,{"disambiguationData":[TD([[makeQuery(id+"F2.imprint","INTERSECT",VERTEX,{"derivedFrom":[subQ2,sQuery(id+"F2.wireOp",EDGE,"E21")]}),1.0]])],"derivedFrom":subQ2})])]}),makeQuery(id+"F3.opExtrude","SWEPT_FACE",FACE,{"disambiguationData":[OSD([subQ1]),TDD([makeQuery(id+"F2.imprint","IMPRINT",EDGE,{"disambiguationData":[TD([[makeQuery(id+"F2.imprint","INTERSECT",VERTEX,{"derivedFrom":[subQ2,sQuery(id+"F2.wireOp",EDGE,"E22")]}),-1.0]])],"derivedFrom":subQ2})])]}),makeQuery(id+"F3.opExtrude","SWEPT_FACE",FACE,{"disambiguationData":[OSD([subQ1]),TDD([makeQuery(id+"F2.imprint","IMPRINT",EDGE,{"disambiguationData":[TD([[makeQuery(id+"F2.imprint","INTERSECT",VERTEX,{"derivedFrom":[subQ2,sQuery(id+"F2.wireOp",EDGE,"E8"),subQ0]}),1.0]])],"derivedFrom":subQ2})])]}),makeQuery(id+"F3.opExtrude","SWEPT_FACE",FACE,{"disambiguationData":[OSD([subQ1]),TDD([makeQuery(id+"F2.imprint","IMPRINT",EDGE,{"disambiguationData":[TD([[makeQuery(id+"F2.imprint","INTERSECT",VERTEX,{"derivedFrom":[subQ2,sQuery(id+"F2.wireOp",EDGE,"E9"),subQ6]}),-1.0]])],"derivedFrom":subQ2})])]}),makeQuery(id+"F3.opExtrude","SWEPT_FACE",FACE,{"disambiguationData":[OSD([subQ1]),TDD([makeQuery(id+"F2.imprint","IMPRINT",EDGE,{"disambiguationData":[TD([[makeQuery(id+"F2.imprint","INTERSECT",VERTEX,{"derivedFrom":[subQ2,sQuery(id+"F2.wireOp",EDGE,"E10"),subQ8]}),1.0]])],"derivedFrom":subQ2})])]})])],"derivedFrom":subQ2});}
            var Q2;
            {var subQ0=sQuery(id+"F2.wireOp",EDGE,"E15");var subQ1=sQuery(id+"F0.wireOp",EDGE,"E3");var subQ2=makeQuery(id+"F1.opExtrude","CAP_EDGE",EDGE,{"disambiguationData":[OSD([subQ1])],"isStart":false});var subQ3=sQuery(id+"F0.wireOp",EDGE,"E1.MirrorCS");var subQ4=sQuery(id+"F0.wireOp",EDGE,"E0");var subQ5=sQuery(id+"F2.wireOp",EDGE,"E9");var subQ6=sQuery(id+"F2.wireOp",EDGE,"E12");var subQ7=sQuery(id+"F2.wireOp",EDGE,"E10");var subQ8=sQuery(id+"F2.wireOp",EDGE,"E18");Q2=makeQuery(id+"F3.boolean.opBoolean","SPLIT",EDGE,{"disambiguationData":[TD([makeQuery(id+"F1.opExtrude","CAP_FACE",FACE,{"disambiguationData":[OSD([subQ4,subQ3,sQuery(id+"F0.wireOp",EDGE,"E2"),subQ1])],"isStart":false}),makeQuery(id+"F1.opExtrude","SWEPT_FACE",FACE,{"disambiguationData":[OSD([subQ1])]}),makeQuery(id+"F3.opExtrude","SWEPT_FACE",FACE,{"disambiguationData":[OSD([subQ5])]}),makeQuery(id+"F3.opExtrude","SWEPT_FACE",FACE,{"disambiguationData":[OSD([subQ7])]}),makeQuery(id+"F3.opExtrude","SWEPT_FACE",FACE,{"disambiguationData":[OSD([subQ1]),TDD([makeQuery(id+"F2.imprint","IMPRINT",EDGE,{"disambiguationData":[TD([[makeQuery(id+"F2.imprint","INTERSECT",VERTEX,{"derivedFrom":[makeQuery(id+"F1.opExtrude","CAP_EDGE",EDGE,{"disambiguationData":[OSD([subQ4])],"isStart":false}),subQ2]}),-1.0]])],"derivedFrom":subQ2})])]}),makeQuery(id+"F3.opExtrude","SWEPT_FACE",FACE,{"disambiguationData":[OSD([subQ1]),TDD([makeQuery(id+"F2.imprint","IMPRINT",EDGE,{"disambiguationData":[TD([[makeQuery(id+"F2.imprint","INTERSECT",VERTEX,{"derivedFrom":[makeQuery(id+"F1.opExtrude","CAP_EDGE",EDGE,{"disambiguationData":[OSD([subQ3])],"isStart":false}),subQ2]}),1.0]])],"derivedFrom":subQ2})])]}),makeQuery(id+"F3.opExtrude","SWEPT_FACE",FACE,{"disambiguationData":[OSD([subQ1]),TDD([makeQuery(id+"F2.imprint","IMPRINT",EDGE,{"disambiguationData":[TD([[makeQuery(id+"F2.imprint","INTERSECT",VERTEX,{"derivedFrom":[subQ2,sQuery(id+"F2.wireOp",EDGE,"E21")]}),1.0]])],"derivedFrom":subQ2})])]}),makeQuery(id+"F3.opExtrude","SWEPT_FACE",FACE,{"disambiguationData":[OSD([subQ1]),TDD([makeQuery(id+"F2.imprint","IMPRINT",EDGE,{"disambiguationData":[TD([[makeQuery(id+"F2.imprint","INTERSECT",VERTEX,{"derivedFrom":[subQ2,sQuery(id+"F2.wireOp",EDGE,"E22")]}),-1.0]])],"derivedFrom":subQ2})])]}),makeQuery(id+"F3.opExtrude","SWEPT_FACE",FACE,{"disambiguationData":[OSD([subQ1]),TDD([makeQuery(id+"F2.imprint","IMPRINT",EDGE,{"disambiguationData":[TD([[makeQuery(id+"F2.imprint","INTERSECT",VERTEX,{"derivedFrom":[subQ2,sQuery(id+"F2.wireOp",EDGE,"E8"),subQ0]}),1.0]])],"derivedFrom":subQ2})])]}),makeQuery(id+"F3.opExtrude","SWEPT_FACE",FACE,{"disambiguationData":[OSD([subQ1]),TDD([makeQuery(id+"F2.imprint","IMPRINT",EDGE,{"disambiguationData":[TD([[makeQuery(id+"F2.imprint","INTERSECT",VERTEX,{"derivedFrom":[subQ2,subQ5,subQ6]}),-1.0]])],"derivedFrom":subQ2})])]}),makeQuery(id+"F3.opExtrude","SWEPT_FACE",FACE,{"disambiguationData":[OSD([subQ1]),TDD([makeQuery(id+"F2.imprint","IMPRINT",EDGE,{"disambiguationData":[TD([[makeQuery(id+"F2.imprint","INTERSECT",VERTEX,{"derivedFrom":[subQ2,subQ7,subQ8]}),1.0]])],"derivedFrom":subQ2})])]})])],"derivedFrom":subQ2});}
            var Q3;
            {var subQ0=sQuery(id+"F2.wireOp",EDGE,"E15");var subQ1=sQuery(id+"F2.wireOp",EDGE,"E8");var subQ2=sQuery(id+"F0.wireOp",EDGE,"E3");var subQ3=makeQuery(id+"F1.opExtrude","CAP_EDGE",EDGE,{"disambiguationData":[OSD([subQ2])],"isStart":false});var subQ4=sQuery(id+"F2.wireOp",EDGE,"E14");var subQ5=sQuery(id+"F4.wireOp",EDGE,"E27");var subQ6=makeQuery(id+"F5.opExtrude","SWEPT_FACE",FACE,{"disambiguationData":[OSD([subQ5])]});var subQ7=sQuery(id+"F4.wireOp",EDGE,"E28");var subQ8=sQuery(id+"F4.wireOp",EDGE,"E25");var subQ9=sQuery(id+"F2.wireOp",EDGE,"E10");var subQ10=sQuery(id+"F2.wireOp",EDGE,"E9");var subQ11=sQuery(id+"F2.wireOp",EDGE,"E12");var subQ12=sQuery(id+"F2.wireOp",EDGE,"E18");var subQ13=makeQuery(id+"F5.opExtrude","CAP_FACE",FACE,{"disambiguationData":[OSD([subQ8,sQuery(id+"F4.wireOp",EDGE,"E26.MirrorCS"),subQ5,subQ7])],"isStart":true});Q3=makeQuery(id+"F6.opChamfer","BLEND_EDGE",EDGE,{"blendedFrom":[makeQuery(id+"F5.boolean.opBoolean","SPLIT",EDGE,{"disambiguationData":[TD([makeQuery(id+"F3.opExtrude","SWEPT_FACE",FACE,{"disambiguationData":[OSD([sQuery(id+"F2.wireOp",EDGE,"E5")])]}),makeQuery(id+"F3.opExtrude","SWEPT_FACE",FACE,{"disambiguationData":[OSD([sQuery(id+"F2.wireOp",EDGE,"E6")])]}),makeQuery(id+"F3.opExtrude","SWEPT_FACE",FACE,{"disambiguationData":[OSD([subQ1])]}),makeQuery(id+"F3.opExtrude","SWEPT_FACE",FACE,{"disambiguationData":[OSD([subQ4])]}),subQ13,subQ6])],"derivedFrom":makeQuery(id+"F5.opExtrude","CAP_EDGE",EDGE,{"disambiguationData":[OSD([subQ5])],"isStart":true})}),makeQuery(id+"F5.boolean.opBoolean","SPLIT",FACE,{"disambiguationData":[TD([makeQuery(id+"F1.opExtrude","SWEPT_FACE",FACE,{"disambiguationData":[OSD([subQ2])]}),makeQuery(id+"F3.opExtrude","SWEPT_FACE",FACE,{"disambiguationData":[OSD([subQ10])]}),makeQuery(id+"F3.opExtrude","SWEPT_FACE",FACE,{"disambiguationData":[OSD([subQ9])]}),makeQuery(id+"F3.opExtrude","SWEPT_FACE",FACE,{"disambiguationData":[OSD([sQuery(id+"F2.wireOp",EDGE,"E13")])]}),makeQuery(id+"F3.opExtrude","SWEPT_FACE",FACE,{"disambiguationData":[OSD([sQuery(id+"F2.wireOp",EDGE,"E17")])]}),makeQuery(id+"F3.opExtrude","SWEPT_FACE",FACE,{"disambiguationData":[OSD([subQ2]),TDD([makeQuery(id+"F2.imprint","IMPRINT",EDGE,{"disambiguationData":[TD([[makeQuery(id+"F2.imprint","INTERSECT",VERTEX,{"derivedFrom":[makeQuery(id+"F1.opExtrude","CAP_EDGE",EDGE,{"disambiguationData":[OSD([sQuery(id+"F0.wireOp",EDGE,"E0")])],"isStart":false}),subQ3]}),-1.0]])],"derivedFrom":subQ3})])]}),makeQuery(id+"F3.opExtrude","SWEPT_FACE",FACE,{"disambiguationData":[OSD([subQ2]),TDD([makeQuery(id+"F2.imprint","IMPRINT",EDGE,{"disambiguationData":[TD([[makeQuery(id+"F2.imprint","INTERSECT",VERTEX,{"derivedFrom":[makeQuery(id+"F1.opExtrude","CAP_EDGE",EDGE,{"disambiguationData":[OSD([sQuery(id+"F0.wireOp",EDGE,"E1.MirrorCS")])],"isStart":false}),subQ3]}),1.0]])],"derivedFrom":subQ3})])]}),makeQuery(id+"F3.opExtrude","SWEPT_FACE",FACE,{"disambiguationData":[OSD([subQ2]),TDD([makeQuery(id+"F2.imprint","IMPRINT",EDGE,{"disambiguationData":[TD([[makeQuery(id+"F2.imprint","INTERSECT",VERTEX,{"derivedFrom":[subQ3,sQuery(id+"F2.wireOp",EDGE,"E21")]}),1.0]])],"derivedFrom":subQ3})])]}),makeQuery(id+"F3.opExtrude","SWEPT_FACE",FACE,{"disambiguationData":[OSD([subQ2]),TDD([makeQuery(id+"F2.imprint","IMPRINT",EDGE,{"disambiguationData":[TD([[makeQuery(id+"F2.imprint","INTERSECT",VERTEX,{"derivedFrom":[subQ3,sQuery(id+"F2.wireOp",EDGE,"E22")]}),-1.0]])],"derivedFrom":subQ3})])]}),makeQuery(id+"F3.opExtrude","SWEPT_FACE",FACE,{"disambiguationData":[OSD([subQ2]),TDD([makeQuery(id+"F2.imprint","IMPRINT",EDGE,{"disambiguationData":[TD([[makeQuery(id+"F2.imprint","INTERSECT",VERTEX,{"derivedFrom":[subQ3,subQ1,subQ0]}),1.0]])],"derivedFrom":subQ3})])]}),makeQuery(id+"F3.opExtrude","SWEPT_FACE",FACE,{"disambiguationData":[OSD([subQ2]),TDD([makeQuery(id+"F2.imprint","IMPRINT",EDGE,{"disambiguationData":[TD([[makeQuery(id+"F2.imprint","INTERSECT",VERTEX,{"derivedFrom":[subQ3,subQ10,subQ11]}),-1.0]])],"derivedFrom":subQ3})])]}),makeQuery(id+"F3.opExtrude","SWEPT_FACE",FACE,{"disambiguationData":[OSD([subQ2]),TDD([makeQuery(id+"F2.imprint","IMPRINT",EDGE,{"disambiguationData":[TD([[makeQuery(id+"F2.imprint","INTERSECT",VERTEX,{"derivedFrom":[subQ3,subQ9,subQ12]}),1.0]])],"derivedFrom":subQ3})])]}),subQ13,subQ6,makeQuery(id+"F5.opExtrude","SWEPT_FACE",FACE,{"disambiguationData":[OSD([subQ7]),TDD([makeQuery(id+"F4.imprint","IMPRINT",EDGE,{"disambiguationData":[TD([[makeQuery(id+"F4.imprint","INTERSECT",VERTEX,{"derivedFrom":[makeQuery(id+"F3.opExtrude","CAP_EDGE",EDGE,{"disambiguationData":[OSD([subQ4])],"isStart":false}),subQ7]}),1.0]])],"derivedFrom":subQ7})])]})])],"derivedFrom":subQ13})],"blendedInto":[makeQuery(id+"F5.boolean.opBoolean","SPLIT",FACE,{"disambiguationData":[TD([makeQuery(id+"F1.opExtrude","SWEPT_FACE",FACE,{"disambiguationData":[OSD([subQ2])]}),makeQuery(id+"F3.opExtrude","SWEPT_FACE",FACE,{"disambiguationData":[OSD([subQ10])]}),makeQuery(id+"F3.opExtrude","SWEPT_FACE",FACE,{"disambiguationData":[OSD([subQ9])]}),makeQuery(id+"F3.opExtrude","SWEPT_FACE",FACE,{"disambiguationData":[OSD([sQuery(id+"F2.wireOp",EDGE,"E13")])]}),makeQuery(id+"F3.opExtrude","SWEPT_FACE",FACE,{"disambiguationData":[OSD([sQuery(id+"F2.wireOp",EDGE,"E17")])]}),makeQuery(id+"F3.opExtrude","SWEPT_FACE",FACE,{"disambiguationData":[OSD([subQ2]),TDD([makeQuery(id+"F2.imprint","IMPRINT",EDGE,{"disambiguationData":[TD([[makeQuery(id+"F2.imprint","INTERSECT",VERTEX,{"derivedFrom":[makeQuery(id+"F1.opExtrude","CAP_EDGE",EDGE,{"disambiguationData":[OSD([sQuery(id+"F0.wireOp",EDGE,"E0")])],"isStart":false}),subQ3]}),-1.0]])],"derivedFrom":subQ3})])]}),makeQuery(id+"F3.opExtrude","SWEPT_FACE",FACE,{"disambiguationData":[OSD([subQ2]),TDD([makeQuery(id+"F2.imprint","IMPRINT",EDGE,{"disambiguationData":[TD([[makeQuery(id+"F2.imprint","INTERSECT",VERTEX,{"derivedFrom":[makeQuery(id+"F1.opExtrude","CAP_EDGE",EDGE,{"disambiguationData":[OSD([sQuery(id+"F0.wireOp",EDGE,"E1.MirrorCS")])],"isStart":false}),subQ3]}),1.0]])],"derivedFrom":subQ3})])]}),makeQuery(id+"F3.opExtrude","SWEPT_FACE",FACE,{"disambiguationData":[OSD([subQ2]),TDD([makeQuery(id+"F2.imprint","IMPRINT",EDGE,{"disambiguationData":[TD([[makeQuery(id+"F2.imprint","INTERSECT",VERTEX,{"derivedFrom":[subQ3,sQuery(id+"F2.wireOp",EDGE,"E21")]}),1.0]])],"derivedFrom":subQ3})])]}),makeQuery(id+"F3.opExtrude","SWEPT_FACE",FACE,{"disambiguationData":[OSD([subQ2]),TDD([makeQuery(id+"F2.imprint","IMPRINT",EDGE,{"disambiguationData":[TD([[makeQuery(id+"F2.imprint","INTERSECT",VERTEX,{"derivedFrom":[subQ3,sQuery(id+"F2.wireOp",EDGE,"E22")]}),-1.0]])],"derivedFrom":subQ3})])]}),makeQuery(id+"F3.opExtrude","SWEPT_FACE",FACE,{"disambiguationData":[OSD([subQ2]),TDD([makeQuery(id+"F2.imprint","IMPRINT",EDGE,{"disambiguationData":[TD([[makeQuery(id+"F2.imprint","INTERSECT",VERTEX,{"derivedFrom":[subQ3,subQ1,subQ0]}),1.0]])],"derivedFrom":subQ3})])]}),makeQuery(id+"F3.opExtrude","SWEPT_FACE",FACE,{"disambiguationData":[OSD([subQ2]),TDD([makeQuery(id+"F2.imprint","IMPRINT",EDGE,{"disambiguationData":[TD([[makeQuery(id+"F2.imprint","INTERSECT",VERTEX,{"derivedFrom":[subQ3,subQ10,subQ11]}),-1.0]])],"derivedFrom":subQ3})])]}),makeQuery(id+"F3.opExtrude","SWEPT_FACE",FACE,{"disambiguationData":[OSD([subQ2]),TDD([makeQuery(id+"F2.imprint","IMPRINT",EDGE,{"disambiguationData":[TD([[makeQuery(id+"F2.imprint","INTERSECT",VERTEX,{"derivedFrom":[subQ3,subQ9,subQ12]}),1.0]])],"derivedFrom":subQ3})])]}),subQ13,subQ6,makeQuery(id+"F5.opExtrude","SWEPT_FACE",FACE,{"disambiguationData":[OSD([subQ7]),TDD([makeQuery(id+"F4.imprint","IMPRINT",EDGE,{"disambiguationData":[TD([[makeQuery(id+"F4.imprint","INTERSECT",VERTEX,{"derivedFrom":[makeQuery(id+"F3.opExtrude","CAP_EDGE",EDGE,{"disambiguationData":[OSD([subQ4])],"isStart":false}),subQ7]}),1.0]])],"derivedFrom":subQ7})])]})])],"derivedFrom":subQ13})]});}
            chamfer(context, id + "F9", {"entities" : qUnion([Q0, Q1, Q2, Q3]), "width" : 2.54 * mm, "tangentPropagation" : true});
        }
        {
            var Q0;
            {var subQ0=sQuery(id+"F2.wireOp",EDGE,"E11");var subQ1=makeQuery(id+"F3.opExtrude","SWEPT_FACE",FACE,{"disambiguationData":[OSD([subQ0])]});var subQ2=sQuery(id+"F0.wireOp",EDGE,"E2");var subQ3=makeQuery(id+"F1.opExtrude","CAP_EDGE",EDGE,{"disambiguationData":[OSD([subQ2])],"isStart":false});var subQ4=sQuery(id+"F0.wireOp",EDGE,"E1.MirrorCS");var subQ5=makeQuery(id+"F1.opExtrude","CAP_EDGE",EDGE,{"disambiguationData":[OSD([subQ4])],"isStart":false});var subQ7=sQuery(id+"F2.wireOp",EDGE,"E8");var subQ8=sQuery(id+"F2.wireOp",EDGE,"E14");var subQ9=makeQuery(id+"F3.opExtrude","SWEPT_FACE",FACE,{"disambiguationData":[OSD([subQ8])]});var subQ10=sQuery(id+"F2.wireOp",EDGE,"E22");var subQ12=sQuery(id+"F0.wireOp",EDGE,"E0");var subQ13=makeQuery(id+"F1.opExtrude","CAP_EDGE",EDGE,{"disambiguationData":[OSD([subQ12])],"isStart":false});var subQ15=sQuery(id+"F0.wireOp",EDGE,"E3");var subQ16=makeQuery(id+"F1.opExtrude","CAP_FACE",FACE,{"disambiguationData":[OSD([subQ12,subQ4,subQ2,subQ15])],"isStart":false});var subQ17=sQuery(id+"F2.wireOp",EDGE,"E21");var subQ19=sQuery(id+"F2.wireOp",EDGE,"E15");var subQ20=makeQuery(id+"F1.opExtrude","CAP_EDGE",EDGE,{"disambiguationData":[OSD([subQ15])],"isStart":false});var subQ21=sQuery(id+"F2.wireOp",EDGE,"E12");var subQ22=sQuery(id+"F2.wireOp",EDGE,"E18");Q0=makeQuery(id+"F9.opChamfer","BLEND_EDGE",EDGE,{"blendedFrom":[makeQuery(id+"F3.boolean.opBoolean","SPLIT",EDGE,{"disambiguationData":[TD([subQ16,makeQuery(id+"F1.opExtrude","SWEPT_FACE",FACE,{"disambiguationData":[OSD([subQ15])]}),subQ1,subQ9,makeQuery(id+"F3.opExtrude","SWEPT_FACE",FACE,{"disambiguationData":[OSD([subQ15]),TDD([makeQuery(id+"F2.imprint","IMPRINT",EDGE,{"disambiguationData":[TD([[makeQuery(id+"F2.imprint","INTERSECT",VERTEX,{"derivedFrom":[subQ13,subQ20]}),-1.0]])],"derivedFrom":subQ20})])]}),makeQuery(id+"F3.opExtrude","SWEPT_FACE",FACE,{"disambiguationData":[OSD([subQ15]),TDD([makeQuery(id+"F2.imprint","IMPRINT",EDGE,{"disambiguationData":[TD([[makeQuery(id+"F2.imprint","INTERSECT",VERTEX,{"derivedFrom":[subQ5,subQ20]}),1.0]])],"derivedFrom":subQ20})])]}),makeQuery(id+"F3.opExtrude","SWEPT_FACE",FACE,{"disambiguationData":[OSD([subQ15]),TDD([makeQuery(id+"F2.imprint","IMPRINT",EDGE,{"disambiguationData":[TD([[makeQuery(id+"F2.imprint","INTERSECT",VERTEX,{"derivedFrom":[subQ20,subQ17]}),1.0]])],"derivedFrom":subQ20})])]}),makeQuery(id+"F3.opExtrude","SWEPT_FACE",FACE,{"disambiguationData":[OSD([subQ15]),TDD([makeQuery(id+"F2.imprint","IMPRINT",EDGE,{"disambiguationData":[TD([[makeQuery(id+"F2.imprint","INTERSECT",VERTEX,{"derivedFrom":[subQ20,subQ10]}),-1.0]])],"derivedFrom":subQ20})])]}),makeQuery(id+"F3.opExtrude","SWEPT_FACE",FACE,{"disambiguationData":[OSD([subQ15]),TDD([makeQuery(id+"F2.imprint","IMPRINT",EDGE,{"disambiguationData":[TD([[makeQuery(id+"F2.imprint","INTERSECT",VERTEX,{"derivedFrom":[subQ20,subQ7,subQ19]}),1.0]])],"derivedFrom":subQ20})])]}),makeQuery(id+"F3.opExtrude","SWEPT_FACE",FACE,{"disambiguationData":[OSD([subQ15]),TDD([makeQuery(id+"F2.imprint","IMPRINT",EDGE,{"disambiguationData":[TD([[makeQuery(id+"F2.imprint","INTERSECT",VERTEX,{"derivedFrom":[subQ20,sQuery(id+"F2.wireOp",EDGE,"E9"),subQ21]}),-1.0]])],"derivedFrom":subQ20})])]}),makeQuery(id+"F3.opExtrude","SWEPT_FACE",FACE,{"disambiguationData":[OSD([subQ15]),TDD([makeQuery(id+"F2.imprint","IMPRINT",EDGE,{"disambiguationData":[TD([[makeQuery(id+"F2.imprint","INTERSECT",VERTEX,{"derivedFrom":[subQ20,sQuery(id+"F2.wireOp",EDGE,"E10"),subQ22]}),1.0]])],"derivedFrom":subQ20})])]})])],"derivedFrom":subQ20}),makeQuery(id+"F8.opChamfer","BLEND_FACE",FACE,{"disambiguationData":[OSD([subQ2]),TDD([makeQuery(id+"F3.boolean.opBoolean","SPLIT",EDGE,{"disambiguationData":[TD([subQ16,makeQuery(id+"F1.opExtrude","SWEPT_FACE",FACE,{"disambiguationData":[OSD([subQ2])]}),makeQuery(id+"F3.opExtrude","SWEPT_FACE",FACE,{"disambiguationData":[OSD([subQ7])]}),subQ1,makeQuery(id+"F3.opExtrude","SWEPT_FACE",FACE,{"disambiguationData":[OSD([sQuery(id+"F2.wireOp",EDGE,"E13")])]}),subQ9,makeQuery(id+"F3.opExtrude","SWEPT_FACE",FACE,{"disambiguationData":[OSD([subQ2]),TDD([makeQuery(id+"F2.imprint","IMPRINT",EDGE,{"disambiguationData":[TD([[makeQuery(id+"F2.imprint","INTERSECT",VERTEX,{"derivedFrom":[subQ13,subQ3]}),-1.0]])],"derivedFrom":subQ3})])]}),makeQuery(id+"F3.opExtrude","SWEPT_FACE",FACE,{"disambiguationData":[OSD([subQ2]),TDD([makeQuery(id+"F2.imprint","IMPRINT",EDGE,{"disambiguationData":[TD([[makeQuery(id+"F2.imprint","INTERSECT",VERTEX,{"derivedFrom":[subQ5,subQ3]}),1.0]])],"derivedFrom":subQ3})])]}),makeQuery(id+"F3.opExtrude","SWEPT_FACE",FACE,{"disambiguationData":[OSD([subQ2]),TDD([makeQuery(id+"F2.imprint","IMPRINT",EDGE,{"disambiguationData":[TD([[makeQuery(id+"F2.imprint","INTERSECT",VERTEX,{"derivedFrom":[subQ3,subQ17]}),1.0]])],"derivedFrom":subQ3})])]}),makeQuery(id+"F3.opExtrude","SWEPT_FACE",FACE,{"disambiguationData":[OSD([subQ2]),TDD([makeQuery(id+"F2.imprint","IMPRINT",EDGE,{"disambiguationData":[TD([[makeQuery(id+"F2.imprint","INTERSECT",VERTEX,{"derivedFrom":[subQ3,subQ10]}),-1.0]])],"derivedFrom":subQ3})])]})])],"derivedFrom":subQ3})])]})],"blendedInto":[makeQuery(id+"F8.opChamfer","BLEND_FACE",FACE,{"disambiguationData":[OSD([subQ2]),TDD([makeQuery(id+"F3.boolean.opBoolean","SPLIT",EDGE,{"disambiguationData":[TD([subQ16,makeQuery(id+"F1.opExtrude","SWEPT_FACE",FACE,{"disambiguationData":[OSD([subQ2])]}),makeQuery(id+"F3.opExtrude","SWEPT_FACE",FACE,{"disambiguationData":[OSD([subQ7])]}),subQ1,makeQuery(id+"F3.opExtrude","SWEPT_FACE",FACE,{"disambiguationData":[OSD([sQuery(id+"F2.wireOp",EDGE,"E13")])]}),subQ9,makeQuery(id+"F3.opExtrude","SWEPT_FACE",FACE,{"disambiguationData":[OSD([subQ2]),TDD([makeQuery(id+"F2.imprint","IMPRINT",EDGE,{"disambiguationData":[TD([[makeQuery(id+"F2.imprint","INTERSECT",VERTEX,{"derivedFrom":[subQ13,subQ3]}),-1.0]])],"derivedFrom":subQ3})])]}),makeQuery(id+"F3.opExtrude","SWEPT_FACE",FACE,{"disambiguationData":[OSD([subQ2]),TDD([makeQuery(id+"F2.imprint","IMPRINT",EDGE,{"disambiguationData":[TD([[makeQuery(id+"F2.imprint","INTERSECT",VERTEX,{"derivedFrom":[subQ5,subQ3]}),1.0]])],"derivedFrom":subQ3})])]}),makeQuery(id+"F3.opExtrude","SWEPT_FACE",FACE,{"disambiguationData":[OSD([subQ2]),TDD([makeQuery(id+"F2.imprint","IMPRINT",EDGE,{"disambiguationData":[TD([[makeQuery(id+"F2.imprint","INTERSECT",VERTEX,{"derivedFrom":[subQ3,subQ17]}),1.0]])],"derivedFrom":subQ3})])]}),makeQuery(id+"F3.opExtrude","SWEPT_FACE",FACE,{"disambiguationData":[OSD([subQ2]),TDD([makeQuery(id+"F2.imprint","IMPRINT",EDGE,{"disambiguationData":[TD([[makeQuery(id+"F2.imprint","INTERSECT",VERTEX,{"derivedFrom":[subQ3,subQ10]}),-1.0]])],"derivedFrom":subQ3})])]})])],"derivedFrom":subQ3})])]})]});}
            var Q1;
            {var subQ0=sQuery(id+"F4.wireOp",EDGE,"E27");var subQ5=sQuery(id+"F2.wireOp",EDGE,"E11");var subQ8=sQuery(id+"F2.wireOp",EDGE,"E14");var subQ9=sQuery(id+"F4.wireOp",EDGE,"E28");var subQ10=makeQuery(id+"F4.imprint","INTERSECT",VERTEX,{"derivedFrom":[makeQuery(id+"F3.opExtrude","CAP_EDGE",EDGE,{"disambiguationData":[OSD([subQ8])],"isStart":false}),subQ9]});var subQ12=makeQuery(id+"F4.imprint","IMPRINT",EDGE,{"disambiguationData":[TD([[subQ10,1.0]])],"derivedFrom":subQ9});Q1=makeQuery(id+"F9.opChamfer","BLEND_EDGE",EDGE,{"blendedFrom":[makeQuery(id+"F5.boolean.opBoolean","SPLIT",EDGE,{"disambiguationData":[TD([makeQuery(id+"F3.opExtrude","SWEPT_FACE",FACE,{"disambiguationData":[OSD([subQ5])]})])],"derivedFrom":makeQuery(id+"F5.opExtrude","CAP_EDGE",EDGE,{"disambiguationData":[OSD([subQ9]),TDD([subQ12])],"isStart":true})}),makeQuery(id+"F6.opChamfer","BLEND_FACE",FACE,{"disambiguationData":[OSD([subQ0]),OD(2.0)]})],"blendedInto":[makeQuery(id+"F6.opChamfer","BLEND_FACE",FACE,{"disambiguationData":[OSD([subQ0]),OD(2.0)]})]});}
            var Q2;
            {var subQ0=sQuery(id+"F2.wireOp",EDGE,"E10");var subQ1=makeQuery(id+"F3.opExtrude","SWEPT_FACE",FACE,{"disambiguationData":[OSD([subQ0])]});var subQ2=sQuery(id+"F0.wireOp",EDGE,"E3");var subQ3=sQuery(id+"F0.wireOp",EDGE,"E2");var subQ4=sQuery(id+"F0.wireOp",EDGE,"E1.MirrorCS");var subQ5=sQuery(id+"F0.wireOp",EDGE,"E0");var subQ6=makeQuery(id+"F1.opExtrude","CAP_FACE",FACE,{"disambiguationData":[OSD([subQ5,subQ4,subQ3,subQ2])],"isStart":false});var subQ7=makeQuery(id+"F1.opExtrude","CAP_EDGE",EDGE,{"disambiguationData":[OSD([subQ3])],"isStart":false});var subQ8=makeQuery(id+"F1.opExtrude","CAP_EDGE",EDGE,{"disambiguationData":[OSD([subQ5])],"isStart":false});var subQ10=sQuery(id+"F2.wireOp",EDGE,"E9");var subQ11=makeQuery(id+"F3.opExtrude","SWEPT_FACE",FACE,{"disambiguationData":[OSD([subQ10])]});var subQ12=sQuery(id+"F2.wireOp",EDGE,"E21");var subQ14=makeQuery(id+"F1.opExtrude","CAP_EDGE",EDGE,{"disambiguationData":[OSD([subQ4])],"isStart":false});var subQ16=sQuery(id+"F2.wireOp",EDGE,"E22");var subQ18=sQuery(id+"F2.wireOp",EDGE,"E15");var subQ19=makeQuery(id+"F1.opExtrude","CAP_EDGE",EDGE,{"disambiguationData":[OSD([subQ2])],"isStart":false});var subQ20=sQuery(id+"F2.wireOp",EDGE,"E12");var subQ21=sQuery(id+"F2.wireOp",EDGE,"E18");Q2=makeQuery(id+"F9.opChamfer","BLEND_EDGE",EDGE,{"blendedFrom":[makeQuery(id+"F3.boolean.opBoolean","SPLIT",EDGE,{"disambiguationData":[TD([subQ6,makeQuery(id+"F1.opExtrude","SWEPT_FACE",FACE,{"disambiguationData":[OSD([subQ2])]}),subQ11,subQ1,makeQuery(id+"F3.opExtrude","SWEPT_FACE",FACE,{"disambiguationData":[OSD([subQ2]),TDD([makeQuery(id+"F2.imprint","IMPRINT",EDGE,{"disambiguationData":[TD([[makeQuery(id+"F2.imprint","INTERSECT",VERTEX,{"derivedFrom":[subQ8,subQ19]}),-1.0]])],"derivedFrom":subQ19})])]}),makeQuery(id+"F3.opExtrude","SWEPT_FACE",FACE,{"disambiguationData":[OSD([subQ2]),TDD([makeQuery(id+"F2.imprint","IMPRINT",EDGE,{"disambiguationData":[TD([[makeQuery(id+"F2.imprint","INTERSECT",VERTEX,{"derivedFrom":[subQ14,subQ19]}),1.0]])],"derivedFrom":subQ19})])]}),makeQuery(id+"F3.opExtrude","SWEPT_FACE",FACE,{"disambiguationData":[OSD([subQ2]),TDD([makeQuery(id+"F2.imprint","IMPRINT",EDGE,{"disambiguationData":[TD([[makeQuery(id+"F2.imprint","INTERSECT",VERTEX,{"derivedFrom":[subQ19,subQ12]}),1.0]])],"derivedFrom":subQ19})])]}),makeQuery(id+"F3.opExtrude","SWEPT_FACE",FACE,{"disambiguationData":[OSD([subQ2]),TDD([makeQuery(id+"F2.imprint","IMPRINT",EDGE,{"disambiguationData":[TD([[makeQuery(id+"F2.imprint","INTERSECT",VERTEX,{"derivedFrom":[subQ19,subQ16]}),-1.0]])],"derivedFrom":subQ19})])]}),makeQuery(id+"F3.opExtrude","SWEPT_FACE",FACE,{"disambiguationData":[OSD([subQ2]),TDD([makeQuery(id+"F2.imprint","IMPRINT",EDGE,{"disambiguationData":[TD([[makeQuery(id+"F2.imprint","INTERSECT",VERTEX,{"derivedFrom":[subQ19,sQuery(id+"F2.wireOp",EDGE,"E8"),subQ18]}),1.0]])],"derivedFrom":subQ19})])]}),makeQuery(id+"F3.opExtrude","SWEPT_FACE",FACE,{"disambiguationData":[OSD([subQ2]),TDD([makeQuery(id+"F2.imprint","IMPRINT",EDGE,{"disambiguationData":[TD([[makeQuery(id+"F2.imprint","INTERSECT",VERTEX,{"derivedFrom":[subQ19,subQ10,subQ20]}),-1.0]])],"derivedFrom":subQ19})])]}),makeQuery(id+"F3.opExtrude","SWEPT_FACE",FACE,{"disambiguationData":[OSD([subQ2]),TDD([makeQuery(id+"F2.imprint","IMPRINT",EDGE,{"disambiguationData":[TD([[makeQuery(id+"F2.imprint","INTERSECT",VERTEX,{"derivedFrom":[subQ19,subQ0,subQ21]}),1.0]])],"derivedFrom":subQ19})])]})])],"derivedFrom":subQ19}),makeQuery(id+"F8.opChamfer","BLEND_FACE",FACE,{"disambiguationData":[OSD([subQ3]),TDD([makeQuery(id+"F3.boolean.opBoolean","SPLIT",EDGE,{"disambiguationData":[TD([subQ6,makeQuery(id+"F1.opExtrude","SWEPT_FACE",FACE,{"disambiguationData":[OSD([subQ3])]}),subQ11,subQ1,makeQuery(id+"F3.opExtrude","SWEPT_FACE",FACE,{"disambiguationData":[OSD([sQuery(id+"F2.wireOp",EDGE,"E13")])]}),makeQuery(id+"F3.opExtrude","SWEPT_FACE",FACE,{"disambiguationData":[OSD([sQuery(id+"F2.wireOp",EDGE,"E17")])]}),makeQuery(id+"F3.opExtrude","SWEPT_FACE",FACE,{"disambiguationData":[OSD([subQ3]),TDD([makeQuery(id+"F2.imprint","IMPRINT",EDGE,{"disambiguationData":[TD([[makeQuery(id+"F2.imprint","INTERSECT",VERTEX,{"derivedFrom":[subQ8,subQ7]}),-1.0]])],"derivedFrom":subQ7})])]}),makeQuery(id+"F3.opExtrude","SWEPT_FACE",FACE,{"disambiguationData":[OSD([subQ3]),TDD([makeQuery(id+"F2.imprint","IMPRINT",EDGE,{"disambiguationData":[TD([[makeQuery(id+"F2.imprint","INTERSECT",VERTEX,{"derivedFrom":[subQ14,subQ7]}),1.0]])],"derivedFrom":subQ7})])]}),makeQuery(id+"F3.opExtrude","SWEPT_FACE",FACE,{"disambiguationData":[OSD([subQ3]),TDD([makeQuery(id+"F2.imprint","IMPRINT",EDGE,{"disambiguationData":[TD([[makeQuery(id+"F2.imprint","INTERSECT",VERTEX,{"derivedFrom":[subQ7,subQ12]}),1.0]])],"derivedFrom":subQ7})])]}),makeQuery(id+"F3.opExtrude","SWEPT_FACE",FACE,{"disambiguationData":[OSD([subQ3]),TDD([makeQuery(id+"F2.imprint","IMPRINT",EDGE,{"disambiguationData":[TD([[makeQuery(id+"F2.imprint","INTERSECT",VERTEX,{"derivedFrom":[subQ7,subQ16]}),-1.0]])],"derivedFrom":subQ7})])]})])],"derivedFrom":subQ7})])]})],"blendedInto":[makeQuery(id+"F8.opChamfer","BLEND_FACE",FACE,{"disambiguationData":[OSD([subQ3]),TDD([makeQuery(id+"F3.boolean.opBoolean","SPLIT",EDGE,{"disambiguationData":[TD([subQ6,makeQuery(id+"F1.opExtrude","SWEPT_FACE",FACE,{"disambiguationData":[OSD([subQ3])]}),subQ11,subQ1,makeQuery(id+"F3.opExtrude","SWEPT_FACE",FACE,{"disambiguationData":[OSD([sQuery(id+"F2.wireOp",EDGE,"E13")])]}),makeQuery(id+"F3.opExtrude","SWEPT_FACE",FACE,{"disambiguationData":[OSD([sQuery(id+"F2.wireOp",EDGE,"E17")])]}),makeQuery(id+"F3.opExtrude","SWEPT_FACE",FACE,{"disambiguationData":[OSD([subQ3]),TDD([makeQuery(id+"F2.imprint","IMPRINT",EDGE,{"disambiguationData":[TD([[makeQuery(id+"F2.imprint","INTERSECT",VERTEX,{"derivedFrom":[subQ8,subQ7]}),-1.0]])],"derivedFrom":subQ7})])]}),makeQuery(id+"F3.opExtrude","SWEPT_FACE",FACE,{"disambiguationData":[OSD([subQ3]),TDD([makeQuery(id+"F2.imprint","IMPRINT",EDGE,{"disambiguationData":[TD([[makeQuery(id+"F2.imprint","INTERSECT",VERTEX,{"derivedFrom":[subQ14,subQ7]}),1.0]])],"derivedFrom":subQ7})])]}),makeQuery(id+"F3.opExtrude","SWEPT_FACE",FACE,{"disambiguationData":[OSD([subQ3]),TDD([makeQuery(id+"F2.imprint","IMPRINT",EDGE,{"disambiguationData":[TD([[makeQuery(id+"F2.imprint","INTERSECT",VERTEX,{"derivedFrom":[subQ7,subQ12]}),1.0]])],"derivedFrom":subQ7})])]}),makeQuery(id+"F3.opExtrude","SWEPT_FACE",FACE,{"disambiguationData":[OSD([subQ3]),TDD([makeQuery(id+"F2.imprint","IMPRINT",EDGE,{"disambiguationData":[TD([[makeQuery(id+"F2.imprint","INTERSECT",VERTEX,{"derivedFrom":[subQ7,subQ16]}),-1.0]])],"derivedFrom":subQ7})])]})])],"derivedFrom":subQ7})])]})]});}
            var Q3;
            {var subQ0=sQuery(id+"F4.wireOp",EDGE,"E28");var subQ1=sQuery(id+"F2.wireOp",EDGE,"E14");var subQ2=sQuery(id+"F4.wireOp",EDGE,"E25");var subQ3=makeQuery(id+"F5.opExtrude","SWEPT_FACE",FACE,{"disambiguationData":[OSD([subQ0]),TDD([makeQuery(id+"F4.imprint","IMPRINT",EDGE,{"disambiguationData":[TD([[makeQuery(id+"F4.imprint","INTERSECT",VERTEX,{"derivedFrom":[makeQuery(id+"F3.opExtrude","CAP_EDGE",EDGE,{"disambiguationData":[OSD([subQ1])],"isStart":false}),subQ0]}),1.0]])],"derivedFrom":subQ0})])]});var subQ4=sQuery(id+"F2.wireOp",EDGE,"E15");var subQ5=sQuery(id+"F2.wireOp",EDGE,"E8");var subQ6=sQuery(id+"F0.wireOp",EDGE,"E3");var subQ7=makeQuery(id+"F1.opExtrude","CAP_EDGE",EDGE,{"disambiguationData":[OSD([subQ6])],"isStart":false});var subQ8=sQuery(id+"F4.wireOp",EDGE,"E27");var subQ9=makeQuery(id+"F5.opExtrude","SWEPT_FACE",FACE,{"disambiguationData":[OSD([subQ8])]});var subQ10=sQuery(id+"F2.wireOp",EDGE,"E10");var subQ11=sQuery(id+"F2.wireOp",EDGE,"E9");var subQ12=sQuery(id+"F2.wireOp",EDGE,"E12");var subQ13=sQuery(id+"F2.wireOp",EDGE,"E18");var subQ14=makeQuery(id+"F5.opExtrude","CAP_FACE",FACE,{"disambiguationData":[OSD([subQ2,sQuery(id+"F4.wireOp",EDGE,"E26.MirrorCS"),subQ8,subQ0])],"isStart":true});Q3=makeQuery(id+"F9.opChamfer","BLEND_EDGE",EDGE,{"blendedFrom":[makeQuery(id+"F6.opChamfer","BLEND_EDGE",EDGE,{"blendedFrom":[makeQuery(id+"F5.boolean.opBoolean","SPLIT",EDGE,{"disambiguationData":[TD([makeQuery(id+"F3.opExtrude","SWEPT_FACE",FACE,{"disambiguationData":[OSD([sQuery(id+"F2.wireOp",EDGE,"E5")])]}),makeQuery(id+"F3.opExtrude","SWEPT_FACE",FACE,{"disambiguationData":[OSD([sQuery(id+"F2.wireOp",EDGE,"E6")])]}),makeQuery(id+"F3.opExtrude","SWEPT_FACE",FACE,{"disambiguationData":[OSD([subQ5])]}),makeQuery(id+"F3.opExtrude","SWEPT_FACE",FACE,{"disambiguationData":[OSD([subQ1])]}),subQ14,subQ9])],"derivedFrom":makeQuery(id+"F5.opExtrude","CAP_EDGE",EDGE,{"disambiguationData":[OSD([subQ8])],"isStart":true})}),makeQuery(id+"F5.boolean.opBoolean","SPLIT",FACE,{"disambiguationData":[TD([makeQuery(id+"F1.opExtrude","SWEPT_FACE",FACE,{"disambiguationData":[OSD([subQ6])]}),makeQuery(id+"F3.opExtrude","SWEPT_FACE",FACE,{"disambiguationData":[OSD([subQ11])]}),makeQuery(id+"F3.opExtrude","SWEPT_FACE",FACE,{"disambiguationData":[OSD([subQ10])]}),makeQuery(id+"F3.opExtrude","SWEPT_FACE",FACE,{"disambiguationData":[OSD([sQuery(id+"F2.wireOp",EDGE,"E13")])]}),makeQuery(id+"F3.opExtrude","SWEPT_FACE",FACE,{"disambiguationData":[OSD([sQuery(id+"F2.wireOp",EDGE,"E17")])]}),makeQuery(id+"F3.opExtrude","SWEPT_FACE",FACE,{"disambiguationData":[OSD([subQ6]),TDD([makeQuery(id+"F2.imprint","IMPRINT",EDGE,{"disambiguationData":[TD([[makeQuery(id+"F2.imprint","INTERSECT",VERTEX,{"derivedFrom":[makeQuery(id+"F1.opExtrude","CAP_EDGE",EDGE,{"disambiguationData":[OSD([sQuery(id+"F0.wireOp",EDGE,"E0")])],"isStart":false}),subQ7]}),-1.0]])],"derivedFrom":subQ7})])]}),makeQuery(id+"F3.opExtrude","SWEPT_FACE",FACE,{"disambiguationData":[OSD([subQ6]),TDD([makeQuery(id+"F2.imprint","IMPRINT",EDGE,{"disambiguationData":[TD([[makeQuery(id+"F2.imprint","INTERSECT",VERTEX,{"derivedFrom":[makeQuery(id+"F1.opExtrude","CAP_EDGE",EDGE,{"disambiguationData":[OSD([sQuery(id+"F0.wireOp",EDGE,"E1.MirrorCS")])],"isStart":false}),subQ7]}),1.0]])],"derivedFrom":subQ7})])]}),makeQuery(id+"F3.opExtrude","SWEPT_FACE",FACE,{"disambiguationData":[OSD([subQ6]),TDD([makeQuery(id+"F2.imprint","IMPRINT",EDGE,{"disambiguationData":[TD([[makeQuery(id+"F2.imprint","INTERSECT",VERTEX,{"derivedFrom":[subQ7,sQuery(id+"F2.wireOp",EDGE,"E21")]}),1.0]])],"derivedFrom":subQ7})])]}),makeQuery(id+"F3.opExtrude","SWEPT_FACE",FACE,{"disambiguationData":[OSD([subQ6]),TDD([makeQuery(id+"F2.imprint","IMPRINT",EDGE,{"disambiguationData":[TD([[makeQuery(id+"F2.imprint","INTERSECT",VERTEX,{"derivedFrom":[subQ7,sQuery(id+"F2.wireOp",EDGE,"E22")]}),-1.0]])],"derivedFrom":subQ7})])]}),makeQuery(id+"F3.opExtrude","SWEPT_FACE",FACE,{"disambiguationData":[OSD([subQ6]),TDD([makeQuery(id+"F2.imprint","IMPRINT",EDGE,{"disambiguationData":[TD([[makeQuery(id+"F2.imprint","INTERSECT",VERTEX,{"derivedFrom":[subQ7,subQ5,subQ4]}),1.0]])],"derivedFrom":subQ7})])]}),makeQuery(id+"F3.opExtrude","SWEPT_FACE",FACE,{"disambiguationData":[OSD([subQ6]),TDD([makeQuery(id+"F2.imprint","IMPRINT",EDGE,{"disambiguationData":[TD([[makeQuery(id+"F2.imprint","INTERSECT",VERTEX,{"derivedFrom":[subQ7,subQ11,subQ12]}),-1.0]])],"derivedFrom":subQ7})])]}),makeQuery(id+"F3.opExtrude","SWEPT_FACE",FACE,{"disambiguationData":[OSD([subQ6]),TDD([makeQuery(id+"F2.imprint","IMPRINT",EDGE,{"disambiguationData":[TD([[makeQuery(id+"F2.imprint","INTERSECT",VERTEX,{"derivedFrom":[subQ7,subQ10,subQ13]}),1.0]])],"derivedFrom":subQ7})])]}),subQ14,subQ9,subQ3])],"derivedFrom":subQ14})],"blendedInto":[makeQuery(id+"F5.boolean.opBoolean","SPLIT",FACE,{"disambiguationData":[TD([makeQuery(id+"F1.opExtrude","SWEPT_FACE",FACE,{"disambiguationData":[OSD([subQ6])]}),makeQuery(id+"F3.opExtrude","SWEPT_FACE",FACE,{"disambiguationData":[OSD([subQ11])]}),makeQuery(id+"F3.opExtrude","SWEPT_FACE",FACE,{"disambiguationData":[OSD([subQ10])]}),makeQuery(id+"F3.opExtrude","SWEPT_FACE",FACE,{"disambiguationData":[OSD([sQuery(id+"F2.wireOp",EDGE,"E13")])]}),makeQuery(id+"F3.opExtrude","SWEPT_FACE",FACE,{"disambiguationData":[OSD([sQuery(id+"F2.wireOp",EDGE,"E17")])]}),makeQuery(id+"F3.opExtrude","SWEPT_FACE",FACE,{"disambiguationData":[OSD([subQ6]),TDD([makeQuery(id+"F2.imprint","IMPRINT",EDGE,{"disambiguationData":[TD([[makeQuery(id+"F2.imprint","INTERSECT",VERTEX,{"derivedFrom":[makeQuery(id+"F1.opExtrude","CAP_EDGE",EDGE,{"disambiguationData":[OSD([sQuery(id+"F0.wireOp",EDGE,"E0")])],"isStart":false}),subQ7]}),-1.0]])],"derivedFrom":subQ7})])]}),makeQuery(id+"F3.opExtrude","SWEPT_FACE",FACE,{"disambiguationData":[OSD([subQ6]),TDD([makeQuery(id+"F2.imprint","IMPRINT",EDGE,{"disambiguationData":[TD([[makeQuery(id+"F2.imprint","INTERSECT",VERTEX,{"derivedFrom":[makeQuery(id+"F1.opExtrude","CAP_EDGE",EDGE,{"disambiguationData":[OSD([sQuery(id+"F0.wireOp",EDGE,"E1.MirrorCS")])],"isStart":false}),subQ7]}),1.0]])],"derivedFrom":subQ7})])]}),makeQuery(id+"F3.opExtrude","SWEPT_FACE",FACE,{"disambiguationData":[OSD([subQ6]),TDD([makeQuery(id+"F2.imprint","IMPRINT",EDGE,{"disambiguationData":[TD([[makeQuery(id+"F2.imprint","INTERSECT",VERTEX,{"derivedFrom":[subQ7,sQuery(id+"F2.wireOp",EDGE,"E21")]}),1.0]])],"derivedFrom":subQ7})])]}),makeQuery(id+"F3.opExtrude","SWEPT_FACE",FACE,{"disambiguationData":[OSD([subQ6]),TDD([makeQuery(id+"F2.imprint","IMPRINT",EDGE,{"disambiguationData":[TD([[makeQuery(id+"F2.imprint","INTERSECT",VERTEX,{"derivedFrom":[subQ7,sQuery(id+"F2.wireOp",EDGE,"E22")]}),-1.0]])],"derivedFrom":subQ7})])]}),makeQuery(id+"F3.opExtrude","SWEPT_FACE",FACE,{"disambiguationData":[OSD([subQ6]),TDD([makeQuery(id+"F2.imprint","IMPRINT",EDGE,{"disambiguationData":[TD([[makeQuery(id+"F2.imprint","INTERSECT",VERTEX,{"derivedFrom":[subQ7,subQ5,subQ4]}),1.0]])],"derivedFrom":subQ7})])]}),makeQuery(id+"F3.opExtrude","SWEPT_FACE",FACE,{"disambiguationData":[OSD([subQ6]),TDD([makeQuery(id+"F2.imprint","IMPRINT",EDGE,{"disambiguationData":[TD([[makeQuery(id+"F2.imprint","INTERSECT",VERTEX,{"derivedFrom":[subQ7,subQ11,subQ12]}),-1.0]])],"derivedFrom":subQ7})])]}),makeQuery(id+"F3.opExtrude","SWEPT_FACE",FACE,{"disambiguationData":[OSD([subQ6]),TDD([makeQuery(id+"F2.imprint","IMPRINT",EDGE,{"disambiguationData":[TD([[makeQuery(id+"F2.imprint","INTERSECT",VERTEX,{"derivedFrom":[subQ7,subQ10,subQ13]}),1.0]])],"derivedFrom":subQ7})])]}),subQ14,subQ9,subQ3])],"derivedFrom":subQ14})]}),subQ3],"blendedInto":[subQ3]});}
            chamfer(context, id + "F10", {"entities" : qUnion([Q0, Q1, Q2, Q3]), "width" : 2.54 * mm, "tangentPropagation" : true});
        }
    });
